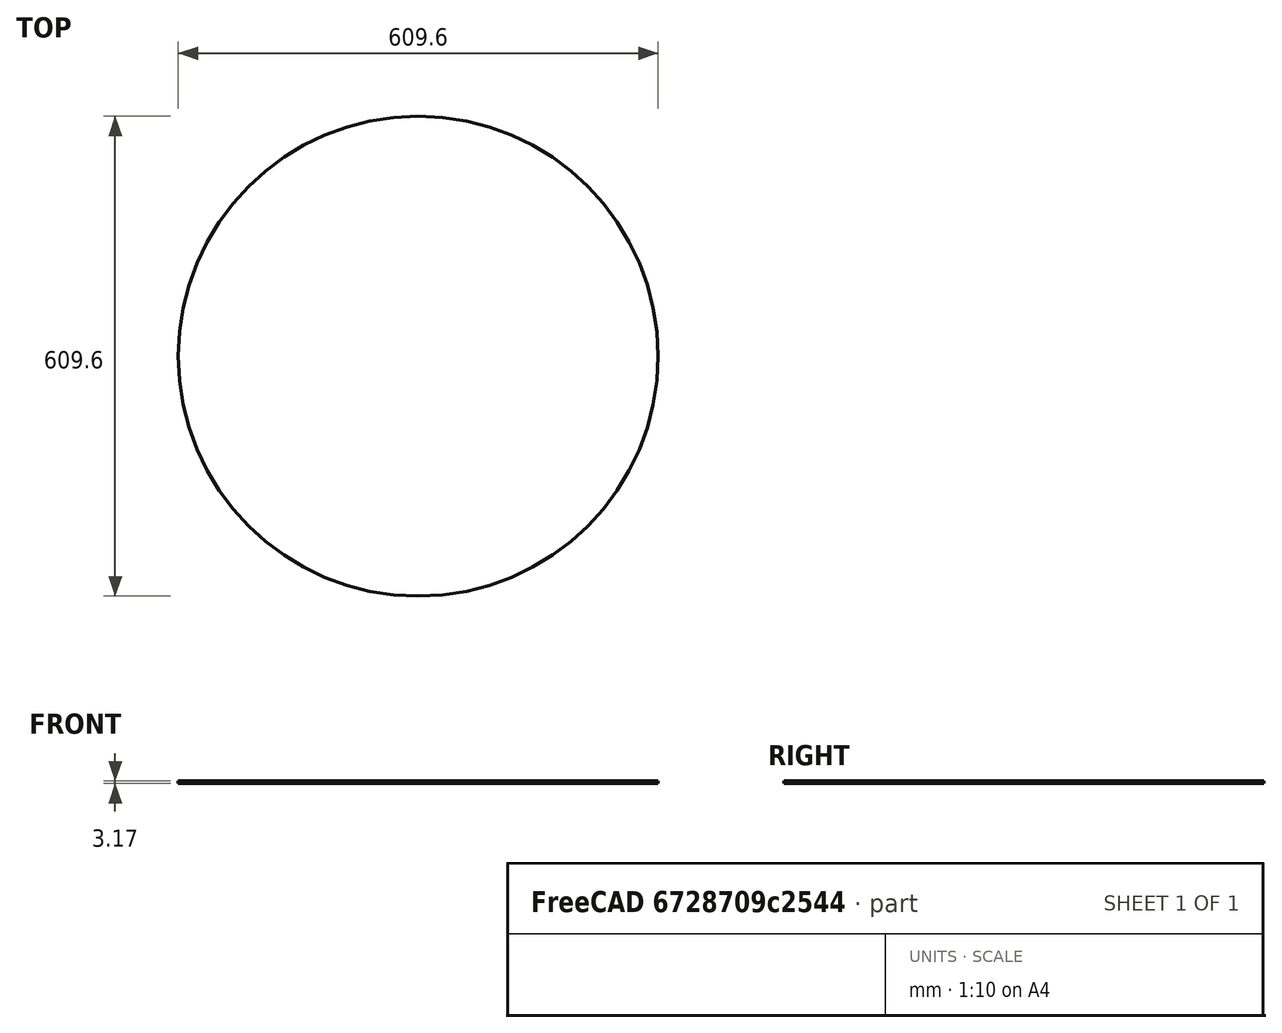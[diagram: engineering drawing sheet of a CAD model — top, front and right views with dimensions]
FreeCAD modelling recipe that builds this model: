
FCSTD DOCUMENT  (FreeCAD 0.15R4671 (Git))
Label: board
License: All rights reserved
LicenseURL: http://en.wikipedia.org/wiki/All_rights_reserved
objects: Sketcher::SketchObject×2, PartDesign::Pad×1
note: 4 computed .brp shape members not serialized (recipe doc carries the construction recipe); baked Part::Feature solids carry a one-line shape summary decoded from their .brp

FEATURE [Sketcher::SketchObject] Sketch001
  sketch-geometry (1):
    g0: Circle CenterX=0 CenterY=0 CenterZ=0 NormalX=0 NormalY=0 NormalZ=1 Radius=304.8
  constraints (2):
    c: Radius(g0) = 304.8
    c: Coincident(g-1,g0)
FEATURE [PartDesign::Pad] Pad
  Length = 3.175
  Length2 = 100
  Sketch = -> Sketch001
  Type = 0
FEATURE [Sketcher::SketchObject] Sketch
  Placement = pos=(0,0,3.175) rot=(0,0,1;0rad)
  Support = -> Pad [Face3]
  sketch-geometry (66):
    g0: Circle [constr] CenterX=0 CenterY=0 CenterZ=0 NormalX=0 NormalY=0 NormalZ=1 Radius=304.8
    g1: LineSegment StartX=-47.625 StartY=-203.2 StartZ=0 EndX=47.625 EndY=-203.2 EndZ=0
    g2: LineSegment StartX=47.625 StartY=-203.2 StartZ=0 EndX=47.625 EndY=-266.7 EndZ=0
    g3: LineSegment StartX=47.625 StartY=-266.7 StartZ=0 EndX=-47.625 EndY=-266.7 EndZ=0
    g4: LineSegment StartX=-47.625 StartY=-266.7 StartZ=0 EndX=-47.625 EndY=-203.2 EndZ=0
    g5: LineSegment StartX=-47.625 StartY=-273.05 StartZ=0 EndX=-28.575 EndY=-273.05 EndZ=0
    g6: LineSegment StartX=-28.575 StartY=-273.05 StartZ=0 EndX=-28.575 EndY=-292.1 EndZ=0
    g7: LineSegment StartX=-28.575 StartY=-292.1 StartZ=0 EndX=-47.625 EndY=-292.1 EndZ=0
    g8: LineSegment StartX=-47.625 StartY=-292.1 StartZ=0 EndX=-47.625 EndY=-273.05 EndZ=0
    g9: LineSegment StartX=-22.225 StartY=-273.05 StartZ=0 EndX=-3.175 EndY=-273.05 EndZ=0
    g10: LineSegment StartX=-3.175 StartY=-273.05 StartZ=0 EndX=-3.175 EndY=-292.1 EndZ=0
    g11: LineSegment StartX=-3.175 StartY=-292.1 StartZ=0 EndX=-22.225 EndY=-292.1 EndZ=0
    g12: LineSegment StartX=-22.225 StartY=-292.1 StartZ=0 EndX=-22.225 EndY=-273.05 EndZ=0
    g13: LineSegment StartX=3.175 StartY=-273.05 StartZ=0 EndX=22.225 EndY=-273.05 EndZ=0
    g14: LineSegment StartX=22.225 StartY=-273.05 StartZ=0 EndX=22.225 EndY=-292.1 EndZ=0
    g15: LineSegment StartX=22.225 StartY=-292.1 StartZ=0 EndX=3.175 EndY=-292.1 EndZ=0
    g16: LineSegment StartX=3.175 StartY=-292.1 StartZ=0 EndX=3.175 EndY=-273.05 EndZ=0
    g17: LineSegment StartX=28.575 StartY=-273.05 StartZ=0 EndX=47.625 EndY=-273.05 EndZ=0
    g18: LineSegment StartX=47.625 StartY=-273.05 StartZ=0 EndX=47.625 EndY=-292.1 EndZ=0
    g19: LineSegment StartX=47.625 StartY=-292.1 StartZ=0 EndX=28.575 EndY=-292.1 EndZ=0
    g20: LineSegment StartX=28.575 StartY=-292.1 StartZ=0 EndX=28.575 EndY=-273.05 EndZ=0
    g21: Circle [constr] CenterX=0 CenterY=0 CenterZ=0 NormalX=0 NormalY=0 NormalZ=1 Radius=101.6
    g22: Circle [constr] CenterX=-79.375 CenterY=-234.95 CenterZ=0 NormalX=0 NormalY=0 NormalZ=1 Radius=20.32
    g23: GeomPoint [constr] X=-47.625 Y=-234.95 Z=0
    g24: LineSegment StartX=53.975 StartY=-209.55 StartZ=0 EndX=73.025 EndY=-209.55 EndZ=0
    g25: LineSegment StartX=73.025 StartY=-209.55 StartZ=0 EndX=73.025 EndY=-228.6 EndZ=0
    g26: LineSegment StartX=73.025 StartY=-228.6 StartZ=0 EndX=53.975 EndY=-228.6 EndZ=0
    g27: LineSegment StartX=53.975 StartY=-228.6 StartZ=0 EndX=53.975 EndY=-209.55 EndZ=0
    g28: LineSegment StartX=53.975 StartY=-241.3 StartZ=0 EndX=73.025 EndY=-241.3 EndZ=0
    g29: LineSegment StartX=73.025 StartY=-241.3 StartZ=0 EndX=73.025 EndY=-260.35 EndZ=0
    g30: LineSegment StartX=73.025 StartY=-260.35 StartZ=0 EndX=53.975 EndY=-260.35 EndZ=0
    g31: LineSegment StartX=53.975 StartY=-260.35 StartZ=0 EndX=53.975 EndY=-241.3 EndZ=0
    g32: LineSegment [constr] StartX=0 StartY=0 StartZ=0 EndX=215.526 EndY=215.526 EndZ=0
    g33: LineSegment [constr] StartX=0 StartY=0 StartZ=0 EndX=215.526 EndY=-215.526 EndZ=0
    g34: LineSegment [constr] StartX=0 StartY=0 StartZ=0 EndX=-215.526 EndY=-215.526 EndZ=0
    g35: LineSegment [constr] StartX=0 StartY=0 StartZ=0 EndX=-215.526 EndY=215.526 EndZ=0
    g36: LineSegment [constr] StartX=0 StartY=0 StartZ=0 EndX=138.376 EndY=-271.579 EndZ=0
    g37: LineSegment [constr] StartX=0 StartY=0 StartZ=0 EndX=-138.376 EndY=-271.579 EndZ=0
    g38: LineSegment [constr] StartX=0 StartY=0 StartZ=0 EndX=-47.6812 EndY=-301.047 EndZ=0
    g39: LineSegment [constr] StartX=0 StartY=0 StartZ=0 EndX=47.6812 EndY=-301.047 EndZ=0
    g40: Circle CenterX=-63.4225 CenterY=-124.474 CenterZ=0 NormalX=0 NormalY=0 NormalZ=1 Radius=15.875
    g41: Circle CenterX=-21.8539 CenterY=-137.98 CenterZ=0 NormalX=0 NormalY=0 NormalZ=1 Radius=15.875
    g42: Circle CenterX=21.8539 CenterY=-137.98 CenterZ=0 NormalX=0 NormalY=0 NormalZ=1 Radius=15.875
    g43: Circle CenterX=63.4225 CenterY=-124.474 CenterZ=0 NormalX=0 NormalY=0 NormalZ=1 Radius=15.875
    g44: Circle CenterX=98.7828 CenterY=-98.7828 CenterZ=0 NormalX=0 NormalY=0 NormalZ=1 Radius=15.875
    g45: Circle CenterX=-98.7828 CenterY=-98.7828 CenterZ=0 NormalX=0 NormalY=0 NormalZ=1 Radius=15.875
    g46: LineSegment [constr] StartX=0 StartY=0 StartZ=0 EndX=179.157 EndY=-246.588 EndZ=0
    g47: LineSegment [constr] StartX=0 StartY=0 StartZ=0 EndX=94.1884 EndY=-289.882 EndZ=0
    g48: LineSegment [constr] StartX=0 StartY=0 StartZ=0 EndX=0 EndY=-304.8 EndZ=0
    g49: LineSegment [constr] StartX=0 StartY=0 StartZ=0 EndX=-94.1884 EndY=-289.882 EndZ=0
    g50: LineSegment [constr] StartX=0 StartY=0 StartZ=0 EndX=-179.157 EndY=-246.588 EndZ=0
    g51: Circle CenterX=104.508 CenterY=-143.843 CenterZ=0 NormalX=0 NormalY=0 NormalZ=1 Radius=21.59
    g52: Circle CenterX=54.9432 CenterY=-169.098 CenterZ=0 NormalX=0 NormalY=0 NormalZ=1 Radius=21.59
    g53: Circle CenterX=0 CenterY=-177.8 CenterZ=0 NormalX=0 NormalY=0 NormalZ=1 Radius=21.59
    g54: Circle CenterX=-54.9432 CenterY=-169.098 CenterZ=0 NormalX=0 NormalY=0 NormalZ=1 Radius=21.59
    g55: Circle CenterX=-104.508 CenterY=-143.843 CenterZ=0 NormalX=0 NormalY=0 NormalZ=1 Radius=21.59
    g56: Circle CenterX=-157.154 CenterY=-157.154 CenterZ=0 NormalX=0 NormalY=0 NormalZ=1 Radius=25.4
    g57: Circle CenterX=-100.899 CenterY=-198.026 CenterZ=0 NormalX=0 NormalY=0 NormalZ=1 Radius=25.4
    g58: Circle CenterX=157.154 CenterY=-157.154 CenterZ=0 NormalX=0 NormalY=0 NormalZ=1 Radius=25.4
    g59: Circle CenterX=100.899 CenterY=-198.026 CenterZ=0 NormalX=0 NormalY=0 NormalZ=1 Radius=25.4
    g60: Circle CenterX=-156.762 CenterY=-215.765 CenterZ=0 NormalX=0 NormalY=0 NormalZ=1 Radius=25.4
    g61: Circle CenterX=156.762 CenterY=-215.765 CenterZ=0 NormalX=0 NormalY=0 NormalZ=1 Radius=25.4
    g62: Circle [constr] CenterX=0 CenterY=0 CenterZ=0 NormalX=0 NormalY=0 NormalZ=1 Radius=139.7
    g63: Circle [constr] CenterX=0 CenterY=0 CenterZ=0 NormalX=0 NormalY=0 NormalZ=1 Radius=177.8
    g64: Circle [constr] CenterX=0 CenterY=0 CenterZ=0 NormalX=0 NormalY=0 NormalZ=1 Radius=222.25
    g65: Circle [constr] CenterX=0 CenterY=0 CenterZ=0 NormalX=0 NormalY=0 NormalZ=1 Radius=266.7
  constraints (193):
    c: Coincident(g0,g-1)
    c: Radius(g0) = 304.8
    c: Coincident(g1,g2)
    c: Coincident(g2,g3)
    c: Coincident(g3,g4)
    c: Coincident(g4,g1)
    c: Horizontal(g1)
    c: Horizontal(g3)
    c: Vertical(g2)
    c: Vertical(g4)
    c: Distance(g1) = 95.25
    c: Distance(g2) = 63.5
    c: Symmetric(g1,g1,g-2)
    c: Coincident(g5,g6)
    c: Coincident(g6,g7)
    c: Coincident(g7,g8)
    c: Coincident(g8,g5)
    c: Horizontal(g5)
    c: Horizontal(g7)
    c: Vertical(g6)
    c: Vertical(g8)
    c: Distance(g5) = 19.05
    c: Coincident(g9,g10)
    c: Coincident(g10,g11)
    c: Coincident(g11,g12)
    c: Coincident(g12,g9)
    c: Horizontal(g9)
    c: Horizontal(g11)
    c: Vertical(g10)
    c: Vertical(g12)
    c: Coincident(g13,g14)
    c: Coincident(g14,g15)
    c: Coincident(g15,g16)
    c: Coincident(g16,g13)
    c: Horizontal(g13)
    c: Horizontal(g15)
    c: Vertical(g14)
    c: Vertical(g16)
    c: Coincident(g17,g18)
    c: Coincident(g18,g19)
    c: Coincident(g19,g20)
    c: Coincident(g20,g17)
    c: Horizontal(g17)
    c: Horizontal(g19)
    c: Vertical(g18)
    c: Vertical(g20)
    c: Equal(g5,g6)
    c: Equal(g6,g9)
    c: Equal(g9,g10)
    c: Equal(g10,g13)
    c: Equal(g13,g14)
    c: Equal(g14,g17)
    c: Equal(g17,g18)
    c: DistanceX(g5,g9) = 6.35
    c: DistanceX(g9,g13) = 6.35
    c: DistanceX(g13,g17) = 6.35
    c: DistanceY(g6,g11) = 0
    c: DistanceY(g10,g15) = 0
    c: DistanceY(g14,g19) = 0
    c: Symmetric(g5,g17,g-2)
    c: Coincident(g21,g-1)
    c: Radius(g21) = 101.6
    c: DistanceY(g2,g17) = -6.35
    c: DistanceY(g-1,g1) = -203.2
    c: Radius(g22) = 20.32
    c: DistanceX(g22,g1) = 31.75
    c: PointOnObject(g23,g4)
    c: Symmetric(g1,g3,g23)
    c: DistanceY(g22,g23) = 0
    c: Coincident(g24,g25)
    c: Coincident(g25,g26)
    c: Coincident(g26,g27)
    c: Coincident(g27,g24)
    c: Horizontal(g24)
    c: Horizontal(g26)
    c: Vertical(g25)
    c: Vertical(g27)
    c: Coincident(g28,g29)
    c: Coincident(g29,g30)
    c: Coincident(g30,g31)
    c: Coincident(g31,g28)
    c: Horizontal(g28)
    c: Horizontal(g30)
    c: Vertical(g29)
    c: Vertical(g31)
    c: Equal(g17,g5)
    c: Equal(g5,g24)
    c: Equal(g24,g25)
    c: Equal(g28,g29)
    c: Equal(g5,g24)
    c: Equal(g5,g28)
    c: DistanceX(g26,g28) = 0
    c: DistanceY(g25,g28) = -12.7
    c: DistanceX(g24,g1) = -6.35
    c: DistanceY(g1,g24) = -6.35
    c: Coincident(g32,g-1)
    c: PointOnObject(g32,g0)
    c: Angle(g32,g-2) = 0.785398
    c: PointOnObject(g33,g0)
    c: Angle(g33,g32) = 1.5708
    c: Coincident(g-1,g33)
    c: Coincident(g34,g-1)
    c: PointOnObject(g34,g0)
    c: Coincident(g35,g-1)
    c: PointOnObject(g35,g0)
    c: Angle(g34,g33) = 1.5708
    c: Angle(g35,g34) = 1.5708
    c: Coincident(g36,g-1)
    c: PointOnObject(g36,g0)
    c: Coincident(g37,g-1)
    c: PointOnObject(g37,g0)
    c: Coincident(g38,g-1)
    c: PointOnObject(g38,g0)
    c: Coincident(g39,g-1)
    c: PointOnObject(g39,g0)
    c: Angle(g36,g33) = 0.314159
    c: Angle(g39,g36) = 0.314159
    c: Angle(g38,g39) = 0.314159
    c: Angle(g37,g38) = 0.314159
    c: PointOnObject(g41,g38)
    c: PointOnObject(g42,g39)
    c: Equal(g40,g41)
    c: Equal(g40,g42)
    c: Equal(g40,g43)
    c: Radius(g40) = 15.875
    c: PointOnObject(g43,g36)
    c: PointOnObject(g44,g33)
    c: PointOnObject(g45,g34)
    c: Equal(g45,g40)
    c: Equal(g40,g44)
    c: Coincident(g46,g-1)
    c: PointOnObject(g46,g0)
    c: Angle(g46,g33) = 0.15708
    c: Coincident(g47,g-1)
    c: PointOnObject(g47,g0)
    c: Angle(g47,g36) = 0.15708
    c: Coincident(g48,g-1)
    c: PointOnObject(g48,g0)
    c: Angle(g48,g39) = 0.15708
    c: Coincident(g49,g-1)
    c: PointOnObject(g49,g0)
    c: Angle(g49,g38) = 0.15708
    c: Coincident(g50,g-1)
    c: PointOnObject(g50,g0)
    c: Angle(g50,g37) = 0.15708
    c: PointOnObject(g51,g46)
    c: PointOnObject(g52,g47)
    c: PointOnObject(g53,g48)
    c: PointOnObject(g54,g49)
    c: PointOnObject(g55,g50)
    c: Radius(g55) = 21.59
    c: Equal(g55,g54)
    c: Equal(g55,g53)
    c: Equal(g55,g52)
    c: Equal(g55,g51)
    c: PointOnObject(g56,g34)
    c: PointOnObject(g57,g37)
    c: PointOnObject(g58,g33)
    c: Radius(g56) = 25.4
    c: Equal(g56,g57)
    c: Equal(g56,g59)
    c: Equal(g56,g58)
    c: Radius(g60) = 25.4
    c: Equal(g60,g61)
    c: Coincident(g62,g-1)
    c: Radius(g62) = 139.7
    c: PointOnObject(g45,g62)
    c: PointOnObject(g40,g62)
    c: PointOnObject(g41,g62)
    c: PointOnObject(g42,g62)
    c: PointOnObject(g43,g62)
    c: PointOnObject(g44,g62)
    c: Coincident(g63,g-1)
    c: PointOnObject(g55,g63)
    c: PointOnObject(g54,g63)
    c: PointOnObject(g53,g63)
    c: PointOnObject(g52,g63)
    c: PointOnObject(g51,g63)
    c: Radius(g63) = 177.8
    c: Coincident(g64,g-1)
    c: Radius(g64) = 222.25
    c: PointOnObject(g56,g64)
    c: PointOnObject(g57,g64)
    c: PointOnObject(g59,g64)
    c: PointOnObject(g58,g64)
    c: Coincident(g65,g-1)
    c: Radius(g65) = 266.7
    c: PointOnObject(g60,g65)
    c: PointOnObject(g61,g65)
    c: PointOnObject(g61,g46)
    c: PointOnObject(g60,g50)
    c: PointOnObject(g40,g37)
    c: PointOnObject(g59,g36)
